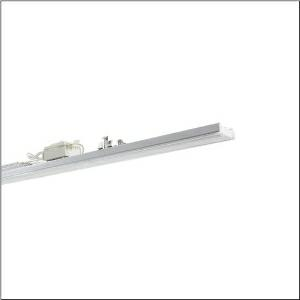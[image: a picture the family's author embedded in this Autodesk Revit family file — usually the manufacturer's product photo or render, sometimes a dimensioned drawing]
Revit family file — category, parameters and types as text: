
# Revit family: licross_11_recessed_mo_51tl12dn195g
name_source: partatom
category: Lighting Fixtures
units: mm (PartAtom-declared; Revit-internal decimal feet)

## family parameters
Cut with Voids When Loaded = No
Host = Face
Light Source = No
Part Type = Normal
Room Calculation Point = No
Round Connector Dimension = Use Diameter
Shared = No

## types (1)
- --- (1 x LED, 9910 lm, 56.7 W, 3500K)
    Apparent Load = 57 VA
    CIE Flux Codes = 67 92 99 100 100
    Color Rendering = 80
    Color Temperature = 3500K
    Default Elevation = 1800 mm
    Description = Licross 11 Recessed MO, luminaire insert, of sheet steel, coil coated, white, length: 1.500mm, width: 66mm, height: 67mm, LED rated luminous flux: 9.910lm, light colour: 835, SDCM (Standard Deviation of Colour Matching)MacAdam ≤ 2 SDCM (initial), control gear: DALI 2, with plug, 5-pole, with phase selection, mains connection: 220..240V, AC, 50/60Hz, rated input power: 57W, internal wiring halogen-free, primary optical cover: cover, of PMMA, light emission: direct distribution, primary light characteristic: symmetric, protection rating (complete): IP40, insulation class (complete): insulation class I (protective earthing), certification: CE, ENEC, VDE, UKCA, protection symbol: D if used in an environment without relevant dust loads with corresponding accessories, impact resistance: IK06, permissible ambient temperature for indoor applications: -25..+35°C, corresponds to IFS (International Featured Standards) requirements for safety and quality in the food industry, reducing of maximum allowable ambient temperature of 5°C with ceiling mounting, LABS conformity tested according to VDMA 24364:2018-05, The light source and the operating device comply with the requirements of the Ecodesign Regulation (EU) 2019/2020 and are replaceable in accordance with this regulation, packaging unit: 1 piece
    Height = 58 mm
    Lamp = 1 x LED
    Lamp Light Flux = 9910 lm
    Lamp Power = 56.7 W
    Lamp count = 1
    Length = 1500 mm
    Luminous efficacy = 175 lm/W
    Manufacturer = Siteco
    ModVariant = No
    Model = 51TL12DN195G
    Mounting Place = Ceiling
    Mounting Type = Pendant
    Number of Poles = 1
    OnlyDefault = Yes
    Power Factor = 1
    Product Name = Licross 11 Recessed MO
    Product group = luminaire insert | ceiling pendant
    ProductGroupID = 901
    Protection Class = Protection class I
    Protection Degree = IP 40
    RLX_Detail_Level = 1
    RLX_Emergency_Light_Flux = 0 lm
    RLX_Emergency_Type = 0
    RLX_Emergency_Type_DB = No
    RlxData = <blob elided: 24609 chars, md5=caf35783>
    Socket = socket
    Standby Power = 0 W
    System Light Flux = 9910 lm
    System Power = 57 W
    Type Comments = factory setting: luminous flux: 100 % | dim-lin: 254 | 378 mA
    Type Image = l_1296930.jpg
    URL = http://relux.com
    VarID = @adj_075623
    Voltage = 0 V
    Weight = 0.00 kg
    Width = 66 mm

## geometry (parser evidence)
native form markers: Blend x4, Sweep x11
no freeform markers — native parametric forms only
